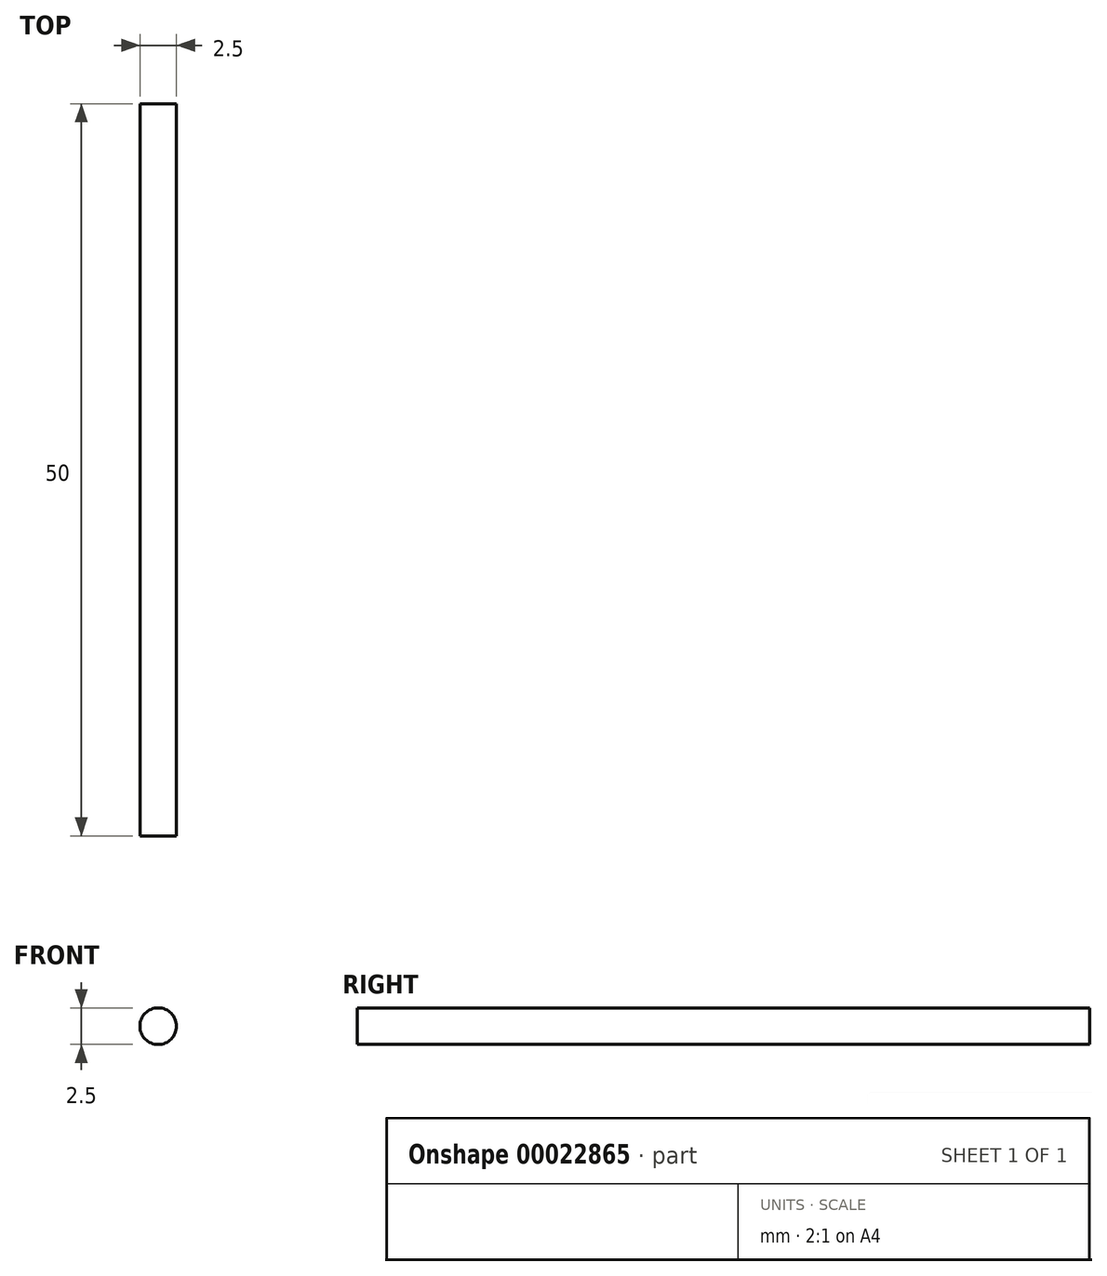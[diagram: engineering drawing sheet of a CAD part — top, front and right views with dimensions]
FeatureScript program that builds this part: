
annotation { "Feature Type Name" : "Feature", "Feature Type Description" : "" }
export const myFeature = defineFeature(function(context is Context, id is Id, definition is map)
    precondition{}
    {
        {
            var Q0;
            Q0=qCreatedBy(makeId("Front.planeOp"),FACE);
            var sketch = newSketch(context, id + "F0", { "sketchPlane" : qUnion([Q0])});
            skCircle(sketch, "E0", {"center": v(0, 0) * mm, "radius": 1.25 * mm});
            skSolve(sketch);
        }
        {
            var Q0;
            Q0=makeQuery(id+"F0.imprint","IMPRINT",FACE,{"disambiguationData":[TD([[makeQuery(id+"F0.imprint","IMPRINT",EDGE,{"derivedFrom":sQuery(id+"F0.wireOp",EDGE,"E0")}),1.0]])]});
            extrude(context, id + "F1", {"entities" : qUnion([Q0]), "depth" : 50 * mm});
        }
    });
